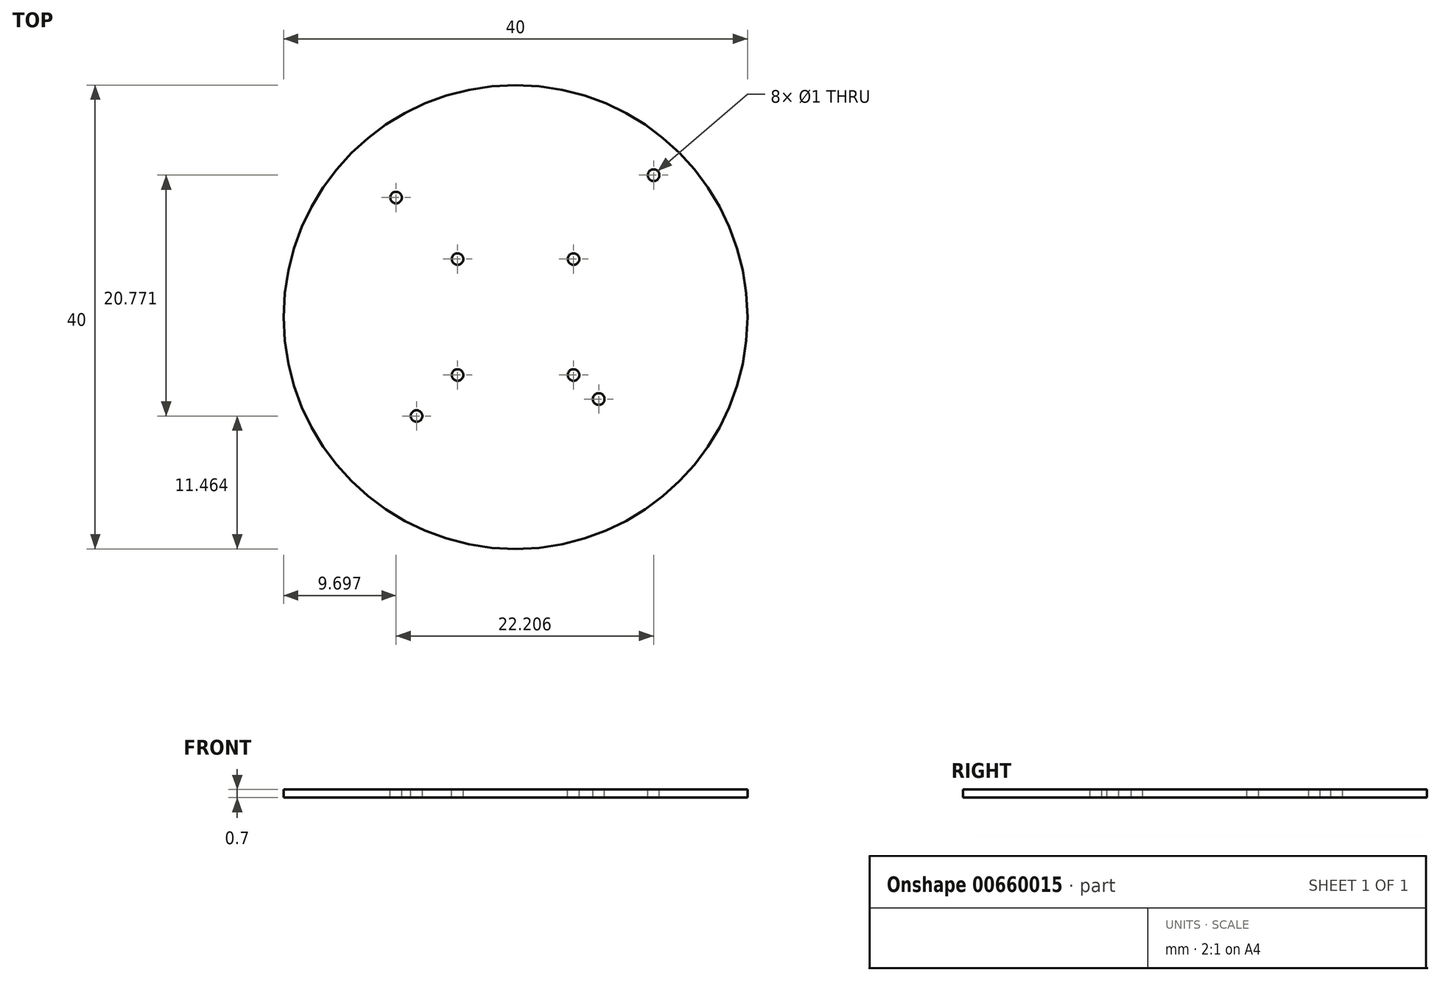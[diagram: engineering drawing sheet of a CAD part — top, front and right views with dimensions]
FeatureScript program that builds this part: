
annotation { "Feature Type Name" : "Feature", "Feature Type Description" : "" }
export const myFeature = defineFeature(function(context is Context, id is Id, definition is map)
    precondition{}
    {
        {
            var Q0;
            Q0=qCreatedBy(makeId("Top.planeOp"),FACE);
            var sketch = newSketch(context, id + "F0", { "sketchPlane" : qUnion([Q0])});
            skCircle(sketch, "E0", {"center": v(0, 0) * mm, "radius": 20 * mm});
            skSolve(sketch);
        }
        {
            var Q0;
            Q0 = qSketchRegion(id + "F0", true);
            extrude(context, id + "F1", {"entities" : qUnion([Q0]), "depth" : .7 * mm, "offsetDistance" : 25 * mm});
        }
        {
            var Q0;
            Q0=makeQuery(id+"F1.opExtrude","CAP_FACE",FACE,{"disambiguationData":[OSD([sQuery(id+"F0.wireOp",EDGE,"E0")])],"isStart":false});
            var sketch = newSketch(context, id + "F2", { "sketchPlane" : qUnion([Q0])});
            skCircle(sketch, "E1", {"center": v(-5, 5) * mm, "radius": 0.5 * mm});
            skCircle(sketch, "E2", {"center": v(5, 5) * mm, "radius": 0.5 * mm});
            skCircle(sketch, "E3", {"center": v(5, -5) * mm, "radius": 0.5 * mm});
            skCircle(sketch, "E4", {"center": v(-5, -5) * mm, "radius": 0.5 * mm});
            skCircle(sketch, "E5", {"center": v(-10.3, 10.3) * mm, "radius": 0.5 * mm});
            skCircle(sketch, "E6", {"center": v(-8.54, -8.54) * mm, "radius": 0.5 * mm});
            skCircle(sketch, "E7", {"center": v(7.17, -7.07) * mm, "radius": 0.5 * mm});
            skCircle(sketch, "E8", {"center": v(11.9, 12.24) * mm, "radius": 0.5 * mm});
            skLineSegment(sketch, "E9", {"start": v(-5, 5) * mm, "end": v(5, -5) * mm});
            skSolve(sketch);
        }
        {
            var Q0;
            Q0 = qSketchRegion(id + "F2", true);
            extrude(context, id + "F3", {"entities" : qUnion([Q0]), "operationType" : NewBodyOperationType.REMOVE, "oppositeDirection" : true, "depth" : .7 * mm, "offsetDistance" : 25 * mm});
        }
    });
